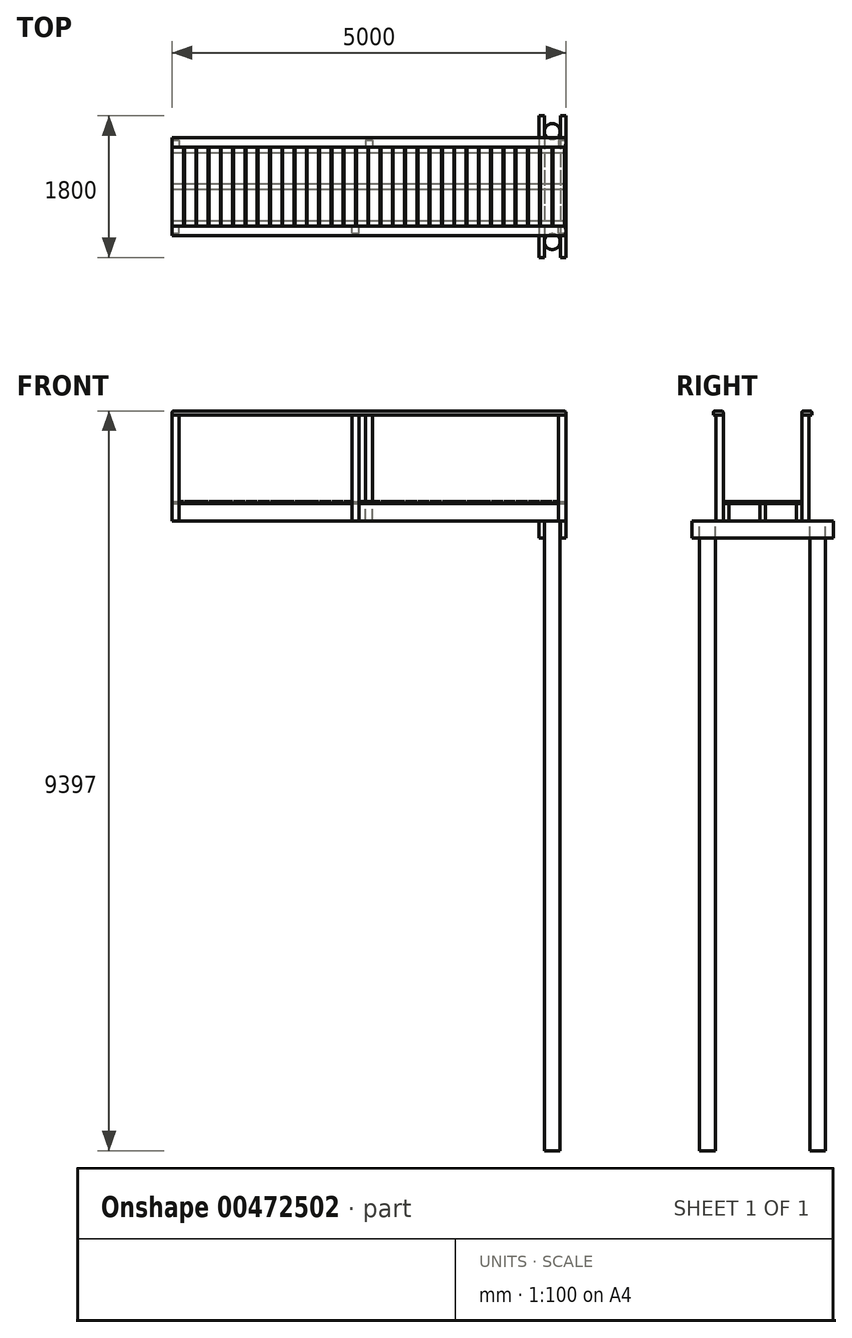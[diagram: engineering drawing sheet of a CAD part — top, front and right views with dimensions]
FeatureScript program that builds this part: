
annotation { "Feature Type Name" : "Feature", "Feature Type Description" : "" }
export const myFeature = defineFeature(function(context is Context, id is Id, definition is map)
    precondition{}
    {
        {
            var Q0;
            Q0=qCreatedBy(makeId("Top.planeOp"),FACE);
            var sketch = newSketch(context, id + "F0", { "sketchPlane" : qUnion([Q0])});
            skCircle(sketch, "E0", {"center": v(-387.32, 554.23) * mm, "radius": 100 * mm});
            skCircle(sketch, "E1", {"center": v(-387.32, -845.77) * mm, "radius": 100 * mm});
            skSolve(sketch);
        }
        {
            var Q0;
            Q0=qCreatedBy(makeId("Top.planeOp"),FACE);
            var sketch = newSketch(context, id + "F1", { "sketchPlane" : qUnion([Q0])});
            skLineSegment(sketch, "E2.bottom", {"start": v(-557.32, 754.23) * mm, "end": v(-487.32, 754.23) * mm});
            skLineSegment(sketch, "E2.top", {"start": v(-557.32, -1045.77) * mm, "end": v(-487.32, -1045.77) * mm});
            skLineSegment(sketch, "E2.left", {"start": v(-557.32, 754.23) * mm, "end": v(-557.32, -1045.77) * mm});
            skLineSegment(sketch, "E2.right", {"start": v(-487.32, 754.23) * mm, "end": v(-487.32, -1045.77) * mm});
            skLineSegment(sketch, "E3.left", {"start": v(-557.32, 754.23) * mm, "end": v(-557.32, 754.23) * mm});
            skLineSegment(sketch, "E3.right", {"start": v(-487.32, 754.23) * mm, "end": v(-487.32, 754.23) * mm});
            skLineSegment(sketch, "E4.MirrorCS", {"start": v(-285.72, 754.23) * mm, "end": v(-285.72, -1045.77) * mm});
            skLineSegment(sketch, "E5.MirrorCS", {"start": v(-215.72, 754.23) * mm, "end": v(-215.72, -1045.77) * mm});
            skLineSegment(sketch, "E6.MirrorCS", {"start": v(-215.72, 754.23) * mm, "end": v(-285.72, 754.23) * mm});
            skLineSegment(sketch, "E7.MirrorCS", {"start": v(-215.72, -1045.77) * mm, "end": v(-285.72, -1045.77) * mm});
            skSolve(sketch);
        }
        {
            var Q0;
            Q0=qSketchRegion(id+"F0",true);
            extrude(context, id + "F2", {"entities" : qUnion([Q0]), "oppositeDirection" : true, "depth" : 8000 * mm});
        }
        {
            var Q0;
            Q0=qSketchRegion(id+"F1",true);
            extrude(context, id + "F3", {"entities" : qUnion([Q0]), "oppositeDirection" : true, "depth" : 220 * mm});
        }
        {
            var Q0;
            Q0=qCreatedBy(makeId("Top.planeOp"),FACE);
            var sketch = newSketch(context, id + "F4", { "sketchPlane" : qUnion([Q0])});
            skLineSegment(sketch, "E8.bottom", {"start": v(-5215.72, 354.23) * mm, "end": v(-215.72, 354.23) * mm});
            skLineSegment(sketch, "E8.top", {"start": v(-5215.72, 284.23) * mm, "end": v(-215.72, 284.23) * mm});
            skLineSegment(sketch, "E8.left", {"start": v(-5215.72, 354.23) * mm, "end": v(-5215.72, 284.23) * mm});
            skLineSegment(sketch, "E8.right", {"start": v(-215.72, 354.23) * mm, "end": v(-215.72, 284.23) * mm});
            skLineSegment(sketch, "E9.0.1.0", {"start": v(-5215.72, -110.77) * mm, "end": v(-215.72, -110.77) * mm});
            skLineSegment(sketch, "E9.0.1.1", {"start": v(-5215.72, -180.77) * mm, "end": v(-215.72, -180.77) * mm});
            skLineSegment(sketch, "E9.0.1.2", {"start": v(-215.72, -110.77) * mm, "end": v(-215.72, -180.77) * mm});
            skLineSegment(sketch, "E9.0.1.3", {"start": v(-5215.72, -110.77) * mm, "end": v(-5215.72, -180.77) * mm});
            skLineSegment(sketch, "E9.0.2.0", {"start": v(-5215.72, -575.77) * mm, "end": v(-215.72, -575.77) * mm});
            skLineSegment(sketch, "E9.0.2.1", {"start": v(-5215.72, -645.77) * mm, "end": v(-215.72, -645.77) * mm});
            skLineSegment(sketch, "E9.0.2.2", {"start": v(-215.72, -575.77) * mm, "end": v(-215.72, -645.77) * mm});
            skLineSegment(sketch, "E9.0.2.3", {"start": v(-5215.72, -575.77) * mm, "end": v(-5215.72, -645.77) * mm});
            skLineSegment(sketch, "E9.direction1", {"start": v(-5387.32, 354.23) * mm, "end": v(-5215.72, 354.23) * mm, "construction": true});
            skLineSegment(sketch, "E9.direction2", {"start": v(-5215.72, 354.23) * mm, "end": v(-5215.72, -110.77) * mm, "construction": true});
            skSolve(sketch);
        }
        {
            var Q0;
            Q0=makeQuery(id+"F4.imprint","IMPRINT",FACE,{"disambiguationData":[TD([[makeQuery(id+"F4.imprint","IMPRINT",EDGE,{"derivedFrom":sQuery(id+"F4.wireOp",EDGE,"E8.bottom")}),-1.0]])]});
            var Q1;
            Q1=makeQuery(id+"F4.imprint","IMPRINT",FACE,{"disambiguationData":[TD([[makeQuery(id+"F4.imprint","IMPRINT",EDGE,{"derivedFrom":sQuery(id+"F4.wireOp",EDGE,"E9.0.2.0")}),-1.0]])]});
            var Q2;
            Q2=makeQuery(id+"F4.imprint","IMPRINT",FACE,{"disambiguationData":[TD([[makeQuery(id+"F4.imprint","IMPRINT",EDGE,{"derivedFrom":sQuery(id+"F4.wireOp",EDGE,"E9.0.1.0")}),-1.0]])]});
            extrude(context, id + "F5", {"entities" : qUnion([Q0, Q1, Q2]), "depth" : 220 * mm});
        }
        {
            var Q0;
            Q0=makeQuery(id+"F5.opExtrude","CAP_FACE",FACE,{"disambiguationData":[OSD([sQuery(id+"F4.wireOp",EDGE,"E8.bottom"),sQuery(id+"F4.wireOp",EDGE,"E8.top"),sQuery(id+"F4.wireOp",EDGE,"E8.left"),sQuery(id+"F4.wireOp",EDGE,"E8.right")])],"isStart":false});
            var sketch = newSketch(context, id + "F6", { "sketchPlane" : qUnion([Q0])});
            skLineSegment(sketch, "E10.bottom", {"start": v(-5215.72, 354.23) * mm, "end": v(-5070.72, 354.23) * mm});
            skLineSegment(sketch, "E10.top", {"start": v(-5215.72, -645.77) * mm, "end": v(-5070.72, -645.77) * mm});
            skLineSegment(sketch, "E10.left", {"start": v(-5215.72, 354.23) * mm, "end": v(-5215.72, -645.77) * mm});
            skLineSegment(sketch, "E10.right", {"start": v(-5070.72, 354.23) * mm, "end": v(-5070.72, -645.77) * mm});
            skLineSegment(sketch, "E11.1.0.0", {"start": v(-4914.72, 354.23) * mm, "end": v(-4914.72, -645.77) * mm});
            skLineSegment(sketch, "E11.1.0.1", {"start": v(-5059.72, 354.23) * mm, "end": v(-4914.72, 354.23) * mm});
            skLineSegment(sketch, "E11.1.0.2", {"start": v(-5059.72, 354.23) * mm, "end": v(-5059.72, -645.77) * mm});
            skLineSegment(sketch, "E11.1.0.3", {"start": v(-5059.72, -645.77) * mm, "end": v(-4914.72, -645.77) * mm});
            skLineSegment(sketch, "E11.2.0.0", {"start": v(-4758.72, 354.23) * mm, "end": v(-4758.72, -645.77) * mm});
            skLineSegment(sketch, "E11.2.0.1", {"start": v(-4903.72, 354.23) * mm, "end": v(-4758.72, 354.23) * mm});
            skLineSegment(sketch, "E11.2.0.2", {"start": v(-4903.72, 354.23) * mm, "end": v(-4903.72, -645.77) * mm});
            skLineSegment(sketch, "E11.2.0.3", {"start": v(-4903.72, -645.77) * mm, "end": v(-4758.72, -645.77) * mm});
            skLineSegment(sketch, "E11.3.0.0", {"start": v(-4602.72, 354.23) * mm, "end": v(-4602.72, -645.77) * mm});
            skLineSegment(sketch, "E11.3.0.1", {"start": v(-4747.72, 354.23) * mm, "end": v(-4602.72, 354.23) * mm});
            skLineSegment(sketch, "E11.3.0.2", {"start": v(-4747.72, 354.23) * mm, "end": v(-4747.72, -645.77) * mm});
            skLineSegment(sketch, "E11.3.0.3", {"start": v(-4747.72, -645.77) * mm, "end": v(-4602.72, -645.77) * mm});
            skLineSegment(sketch, "E11.4.0.0", {"start": v(-4446.72, 354.23) * mm, "end": v(-4446.72, -645.77) * mm});
            skLineSegment(sketch, "E11.4.0.1", {"start": v(-4591.72, 354.23) * mm, "end": v(-4446.72, 354.23) * mm});
            skLineSegment(sketch, "E11.4.0.2", {"start": v(-4591.72, 354.23) * mm, "end": v(-4591.72, -645.77) * mm});
            skLineSegment(sketch, "E11.4.0.3", {"start": v(-4591.72, -645.77) * mm, "end": v(-4446.72, -645.77) * mm});
            skLineSegment(sketch, "E11.5.0.0", {"start": v(-4290.72, 354.23) * mm, "end": v(-4290.72, -645.77) * mm});
            skLineSegment(sketch, "E11.5.0.1", {"start": v(-4435.72, 354.23) * mm, "end": v(-4290.72, 354.23) * mm});
            skLineSegment(sketch, "E11.5.0.2", {"start": v(-4435.72, 354.23) * mm, "end": v(-4435.72, -645.77) * mm});
            skLineSegment(sketch, "E11.5.0.3", {"start": v(-4435.72, -645.77) * mm, "end": v(-4290.72, -645.77) * mm});
            skLineSegment(sketch, "E11.6.0.0", {"start": v(-4134.72, 354.23) * mm, "end": v(-4134.72, -645.77) * mm});
            skLineSegment(sketch, "E11.6.0.1", {"start": v(-4279.72, 354.23) * mm, "end": v(-4134.72, 354.23) * mm});
            skLineSegment(sketch, "E11.6.0.2", {"start": v(-4279.72, 354.23) * mm, "end": v(-4279.72, -645.77) * mm});
            skLineSegment(sketch, "E11.6.0.3", {"start": v(-4279.72, -645.77) * mm, "end": v(-4134.72, -645.77) * mm});
            skLineSegment(sketch, "E11.7.0.0", {"start": v(-3978.72, 354.23) * mm, "end": v(-3978.72, -645.77) * mm});
            skLineSegment(sketch, "E11.7.0.1", {"start": v(-4123.72, 354.23) * mm, "end": v(-3978.72, 354.23) * mm});
            skLineSegment(sketch, "E11.7.0.2", {"start": v(-4123.72, 354.23) * mm, "end": v(-4123.72, -645.77) * mm});
            skLineSegment(sketch, "E11.7.0.3", {"start": v(-4123.72, -645.77) * mm, "end": v(-3978.72, -645.77) * mm});
            skLineSegment(sketch, "E11.8.0.0", {"start": v(-3822.72, 354.23) * mm, "end": v(-3822.72, -645.77) * mm});
            skLineSegment(sketch, "E11.8.0.1", {"start": v(-3967.72, 354.23) * mm, "end": v(-3822.72, 354.23) * mm});
            skLineSegment(sketch, "E11.8.0.2", {"start": v(-3967.72, 354.23) * mm, "end": v(-3967.72, -645.77) * mm});
            skLineSegment(sketch, "E11.8.0.3", {"start": v(-3967.72, -645.77) * mm, "end": v(-3822.72, -645.77) * mm});
            skLineSegment(sketch, "E11.9.0.0", {"start": v(-3666.72, 354.23) * mm, "end": v(-3666.72, -645.77) * mm});
            skLineSegment(sketch, "E11.9.0.1", {"start": v(-3811.72, 354.23) * mm, "end": v(-3666.72, 354.23) * mm});
            skLineSegment(sketch, "E11.9.0.2", {"start": v(-3811.72, 354.23) * mm, "end": v(-3811.72, -645.77) * mm});
            skLineSegment(sketch, "E11.9.0.3", {"start": v(-3811.72, -645.77) * mm, "end": v(-3666.72, -645.77) * mm});
            skLineSegment(sketch, "E11.10.0.0", {"start": v(-3510.72, 354.23) * mm, "end": v(-3510.72, -645.77) * mm});
            skLineSegment(sketch, "E11.10.0.1", {"start": v(-3655.72, 354.23) * mm, "end": v(-3510.72, 354.23) * mm});
            skLineSegment(sketch, "E11.10.0.2", {"start": v(-3655.72, 354.23) * mm, "end": v(-3655.72, -645.77) * mm});
            skLineSegment(sketch, "E11.10.0.3", {"start": v(-3655.72, -645.77) * mm, "end": v(-3510.72, -645.77) * mm});
            skLineSegment(sketch, "E11.11.0.0", {"start": v(-3354.72, 354.23) * mm, "end": v(-3354.72, -645.77) * mm});
            skLineSegment(sketch, "E11.11.0.1", {"start": v(-3499.72, 354.23) * mm, "end": v(-3354.72, 354.23) * mm});
            skLineSegment(sketch, "E11.11.0.2", {"start": v(-3499.72, 354.23) * mm, "end": v(-3499.72, -645.77) * mm});
            skLineSegment(sketch, "E11.11.0.3", {"start": v(-3499.72, -645.77) * mm, "end": v(-3354.72, -645.77) * mm});
            skLineSegment(sketch, "E11.12.0.0", {"start": v(-3198.72, 354.23) * mm, "end": v(-3198.72, -645.77) * mm});
            skLineSegment(sketch, "E11.12.0.1", {"start": v(-3343.72, 354.23) * mm, "end": v(-3198.72, 354.23) * mm});
            skLineSegment(sketch, "E11.12.0.2", {"start": v(-3343.72, 354.23) * mm, "end": v(-3343.72, -645.77) * mm});
            skLineSegment(sketch, "E11.12.0.3", {"start": v(-3343.72, -645.77) * mm, "end": v(-3198.72, -645.77) * mm});
            skLineSegment(sketch, "E11.13.0.0", {"start": v(-3042.72, 354.23) * mm, "end": v(-3042.72, -645.77) * mm});
            skLineSegment(sketch, "E11.13.0.1", {"start": v(-3187.72, 354.23) * mm, "end": v(-3042.72, 354.23) * mm});
            skLineSegment(sketch, "E11.13.0.2", {"start": v(-3187.72, 354.23) * mm, "end": v(-3187.72, -645.77) * mm});
            skLineSegment(sketch, "E11.13.0.3", {"start": v(-3187.72, -645.77) * mm, "end": v(-3042.72, -645.77) * mm});
            skLineSegment(sketch, "E11.14.0.0", {"start": v(-2886.72, 354.23) * mm, "end": v(-2886.72, -645.77) * mm});
            skLineSegment(sketch, "E11.14.0.1", {"start": v(-3031.72, 354.23) * mm, "end": v(-2886.72, 354.23) * mm});
            skLineSegment(sketch, "E11.14.0.2", {"start": v(-3031.72, 354.23) * mm, "end": v(-3031.72, -645.77) * mm});
            skLineSegment(sketch, "E11.14.0.3", {"start": v(-3031.72, -645.77) * mm, "end": v(-2886.72, -645.77) * mm});
            skLineSegment(sketch, "E11.15.0.0", {"start": v(-2730.72, 354.23) * mm, "end": v(-2730.72, -645.77) * mm});
            skLineSegment(sketch, "E11.15.0.1", {"start": v(-2875.72, 354.23) * mm, "end": v(-2730.72, 354.23) * mm});
            skLineSegment(sketch, "E11.15.0.2", {"start": v(-2875.72, 354.23) * mm, "end": v(-2875.72, -645.77) * mm});
            skLineSegment(sketch, "E11.15.0.3", {"start": v(-2875.72, -645.77) * mm, "end": v(-2730.72, -645.77) * mm});
            skLineSegment(sketch, "E11.16.0.0", {"start": v(-2574.72, 354.23) * mm, "end": v(-2574.72, -645.77) * mm});
            skLineSegment(sketch, "E11.16.0.1", {"start": v(-2719.72, 354.23) * mm, "end": v(-2574.72, 354.23) * mm});
            skLineSegment(sketch, "E11.16.0.2", {"start": v(-2719.72, 354.23) * mm, "end": v(-2719.72, -645.77) * mm});
            skLineSegment(sketch, "E11.16.0.3", {"start": v(-2719.72, -645.77) * mm, "end": v(-2574.72, -645.77) * mm});
            skLineSegment(sketch, "E11.17.0.0", {"start": v(-2418.72, 354.23) * mm, "end": v(-2418.72, -645.77) * mm});
            skLineSegment(sketch, "E11.17.0.1", {"start": v(-2563.72, 354.23) * mm, "end": v(-2418.72, 354.23) * mm});
            skLineSegment(sketch, "E11.17.0.2", {"start": v(-2563.72, 354.23) * mm, "end": v(-2563.72, -645.77) * mm});
            skLineSegment(sketch, "E11.17.0.3", {"start": v(-2563.72, -645.77) * mm, "end": v(-2418.72, -645.77) * mm});
            skLineSegment(sketch, "E11.18.0.0", {"start": v(-2262.72, 354.23) * mm, "end": v(-2262.72, -645.77) * mm});
            skLineSegment(sketch, "E11.18.0.1", {"start": v(-2407.72, 354.23) * mm, "end": v(-2262.72, 354.23) * mm});
            skLineSegment(sketch, "E11.18.0.2", {"start": v(-2407.72, 354.23) * mm, "end": v(-2407.72, -645.77) * mm});
            skLineSegment(sketch, "E11.18.0.3", {"start": v(-2407.72, -645.77) * mm, "end": v(-2262.72, -645.77) * mm});
            skLineSegment(sketch, "E11.19.0.0", {"start": v(-2106.72, 354.23) * mm, "end": v(-2106.72, -645.77) * mm});
            skLineSegment(sketch, "E11.19.0.1", {"start": v(-2251.72, 354.23) * mm, "end": v(-2106.72, 354.23) * mm});
            skLineSegment(sketch, "E11.19.0.2", {"start": v(-2251.72, 354.23) * mm, "end": v(-2251.72, -645.77) * mm});
            skLineSegment(sketch, "E11.19.0.3", {"start": v(-2251.72, -645.77) * mm, "end": v(-2106.72, -645.77) * mm});
            skLineSegment(sketch, "E11.20.0.0", {"start": v(-1950.72, 354.23) * mm, "end": v(-1950.72, -645.77) * mm});
            skLineSegment(sketch, "E11.20.0.1", {"start": v(-2095.72, 354.23) * mm, "end": v(-1950.72, 354.23) * mm});
            skLineSegment(sketch, "E11.20.0.2", {"start": v(-2095.72, 354.23) * mm, "end": v(-2095.72, -645.77) * mm});
            skLineSegment(sketch, "E11.20.0.3", {"start": v(-2095.72, -645.77) * mm, "end": v(-1950.72, -645.77) * mm});
            skLineSegment(sketch, "E11.21.0.0", {"start": v(-1794.72, 354.23) * mm, "end": v(-1794.72, -645.77) * mm});
            skLineSegment(sketch, "E11.21.0.1", {"start": v(-1939.72, 354.23) * mm, "end": v(-1794.72, 354.23) * mm});
            skLineSegment(sketch, "E11.21.0.2", {"start": v(-1939.72, 354.23) * mm, "end": v(-1939.72, -645.77) * mm});
            skLineSegment(sketch, "E11.21.0.3", {"start": v(-1939.72, -645.77) * mm, "end": v(-1794.72, -645.77) * mm});
            skLineSegment(sketch, "E11.22.0.0", {"start": v(-1638.72, 354.23) * mm, "end": v(-1638.72, -645.77) * mm});
            skLineSegment(sketch, "E11.22.0.1", {"start": v(-1783.72, 354.23) * mm, "end": v(-1638.72, 354.23) * mm});
            skLineSegment(sketch, "E11.22.0.2", {"start": v(-1783.72, 354.23) * mm, "end": v(-1783.72, -645.77) * mm});
            skLineSegment(sketch, "E11.22.0.3", {"start": v(-1783.72, -645.77) * mm, "end": v(-1638.72, -645.77) * mm});
            skLineSegment(sketch, "E11.23.0.0", {"start": v(-1482.72, 354.23) * mm, "end": v(-1482.72, -645.77) * mm});
            skLineSegment(sketch, "E11.23.0.1", {"start": v(-1627.72, 354.23) * mm, "end": v(-1482.72, 354.23) * mm});
            skLineSegment(sketch, "E11.23.0.2", {"start": v(-1627.72, 354.23) * mm, "end": v(-1627.72, -645.77) * mm});
            skLineSegment(sketch, "E11.23.0.3", {"start": v(-1627.72, -645.77) * mm, "end": v(-1482.72, -645.77) * mm});
            skLineSegment(sketch, "E11.24.0.0", {"start": v(-1326.72, 354.23) * mm, "end": v(-1326.72, -645.77) * mm});
            skLineSegment(sketch, "E11.24.0.1", {"start": v(-1471.72, 354.23) * mm, "end": v(-1326.72, 354.23) * mm});
            skLineSegment(sketch, "E11.24.0.2", {"start": v(-1471.72, 354.23) * mm, "end": v(-1471.72, -645.77) * mm});
            skLineSegment(sketch, "E11.24.0.3", {"start": v(-1471.72, -645.77) * mm, "end": v(-1326.72, -645.77) * mm});
            skLineSegment(sketch, "E11.25.0.0", {"start": v(-1170.72, 354.23) * mm, "end": v(-1170.72, -645.77) * mm});
            skLineSegment(sketch, "E11.25.0.1", {"start": v(-1315.72, 354.23) * mm, "end": v(-1170.72, 354.23) * mm});
            skLineSegment(sketch, "E11.25.0.2", {"start": v(-1315.72, 354.23) * mm, "end": v(-1315.72, -645.77) * mm});
            skLineSegment(sketch, "E11.25.0.3", {"start": v(-1315.72, -645.77) * mm, "end": v(-1170.72, -645.77) * mm});
            skLineSegment(sketch, "E11.26.0.0", {"start": v(-1014.72, 354.23) * mm, "end": v(-1014.72, -645.77) * mm});
            skLineSegment(sketch, "E11.26.0.1", {"start": v(-1159.72, 354.23) * mm, "end": v(-1014.72, 354.23) * mm});
            skLineSegment(sketch, "E11.26.0.2", {"start": v(-1159.72, 354.23) * mm, "end": v(-1159.72, -645.77) * mm});
            skLineSegment(sketch, "E11.26.0.3", {"start": v(-1159.72, -645.77) * mm, "end": v(-1014.72, -645.77) * mm});
            skLineSegment(sketch, "E11.27.0.0", {"start": v(-858.72, 354.23) * mm, "end": v(-858.72, -645.77) * mm});
            skLineSegment(sketch, "E11.27.0.1", {"start": v(-1003.72, 354.23) * mm, "end": v(-858.72, 354.23) * mm});
            skLineSegment(sketch, "E11.27.0.2", {"start": v(-1003.72, 354.23) * mm, "end": v(-1003.72, -645.77) * mm});
            skLineSegment(sketch, "E11.27.0.3", {"start": v(-1003.72, -645.77) * mm, "end": v(-858.72, -645.77) * mm});
            skLineSegment(sketch, "E11.28.0.0", {"start": v(-702.72, 354.23) * mm, "end": v(-702.72, -645.77) * mm});
            skLineSegment(sketch, "E11.28.0.1", {"start": v(-847.72, 354.23) * mm, "end": v(-702.72, 354.23) * mm});
            skLineSegment(sketch, "E11.28.0.2", {"start": v(-847.72, 354.23) * mm, "end": v(-847.72, -645.77) * mm});
            skLineSegment(sketch, "E11.28.0.3", {"start": v(-847.72, -645.77) * mm, "end": v(-702.72, -645.77) * mm});
            skLineSegment(sketch, "E11.29.0.0", {"start": v(-546.72, 354.23) * mm, "end": v(-546.72, -645.77) * mm});
            skLineSegment(sketch, "E11.29.0.1", {"start": v(-691.72, 354.23) * mm, "end": v(-546.72, 354.23) * mm});
            skLineSegment(sketch, "E11.29.0.2", {"start": v(-691.72, 354.23) * mm, "end": v(-691.72, -645.77) * mm});
            skLineSegment(sketch, "E11.29.0.3", {"start": v(-691.72, -645.77) * mm, "end": v(-546.72, -645.77) * mm});
            skLineSegment(sketch, "E11.30.0.0", {"start": v(-390.72, 354.23) * mm, "end": v(-390.72, -645.77) * mm});
            skLineSegment(sketch, "E11.30.0.1", {"start": v(-535.72, 354.23) * mm, "end": v(-390.72, 354.23) * mm});
            skLineSegment(sketch, "E11.30.0.2", {"start": v(-535.72, 354.23) * mm, "end": v(-535.72, -645.77) * mm});
            skLineSegment(sketch, "E11.30.0.3", {"start": v(-535.72, -645.77) * mm, "end": v(-390.72, -645.77) * mm});
            skLineSegment(sketch, "E11.31.0.0", {"start": v(-234.72, 354.23) * mm, "end": v(-234.72, -645.77) * mm});
            skLineSegment(sketch, "E11.31.0.1", {"start": v(-379.72, 354.23) * mm, "end": v(-234.72, 354.23) * mm});
            skLineSegment(sketch, "E11.31.0.2", {"start": v(-379.72, 354.23) * mm, "end": v(-379.72, -645.77) * mm});
            skLineSegment(sketch, "E11.31.0.3", {"start": v(-379.72, -645.77) * mm, "end": v(-234.72, -645.77) * mm});
            skLineSegment(sketch, "E11.direction1", {"start": v(-5070.72, -645.77) * mm, "end": v(-4914.72, -645.77) * mm, "construction": true});
            skSolve(sketch);
        }
        {
            var Q0;
            Q0=qSketchRegion(id+"F6",true);
            extrude(context, id + "F7", {"entities" : qUnion([Q0]), "depth" : 27 * mm});
        }
        {
            var Q0;
            Q0=makeQuery(id+"F5.opExtrude","SWEPT_FACE",FACE,{"disambiguationData":[OSD([sQuery(id+"F4.wireOp",EDGE,"E9.0.2.1")])]});
            var sketch = newSketch(context, id + "F8", { "sketchPlane" : qUnion([Q0])});
            skLineSegment(sketch, "E12.bottom", {"start": v(-5215.72, 0) * mm, "end": v(-5125.72, 0) * mm});
            skLineSegment(sketch, "E12.top", {"start": v(-5215.72, 1347) * mm, "end": v(-5125.72, 1347) * mm});
            skLineSegment(sketch, "E12.left", {"start": v(-5215.72, 0) * mm, "end": v(-5215.72, 1347) * mm});
            skLineSegment(sketch, "E12.right", {"start": v(-5125.72, 0) * mm, "end": v(-5125.72, 1347) * mm});
            skLineSegment(sketch, "E13.bottom", {"start": v(-215.72, 0) * mm, "end": v(-305.72, 0) * mm});
            skLineSegment(sketch, "E13.top", {"start": v(-215.72, 1347) * mm, "end": v(-305.72, 1347) * mm});
            skLineSegment(sketch, "E13.left", {"start": v(-215.72, 0) * mm, "end": v(-215.72, 1347) * mm});
            skLineSegment(sketch, "E13.right", {"start": v(-305.72, 0) * mm, "end": v(-305.72, 1347) * mm});
            skLineSegment(sketch, "E14.bottom", {"start": v(-2932.32, 1347) * mm, "end": v(-2842.32, 1347) * mm});
            skLineSegment(sketch, "E14.top", {"start": v(-2932.32, 0) * mm, "end": v(-2842.32, 0) * mm});
            skLineSegment(sketch, "E14.left", {"start": v(-2842.32, 1347) * mm, "end": v(-2842.32, 0) * mm});
            skLineSegment(sketch, "E14.right", {"start": v(-2932.32, 1347) * mm, "end": v(-2932.32, 0) * mm});
            skSolve(sketch);
        }
        {
            var Q0;
            Q0=qSketchRegion(id+"F8",true);
            extrude(context, id + "F9", {"entities" : qUnion([Q0]), "depth" : 90 * mm});
        }
        {
            var Q0;
            Q0=makeQuery(id+"F5.opExtrude","SWEPT_FACE",FACE,{"disambiguationData":[OSD([sQuery(id+"F4.wireOp",EDGE,"E8.bottom")])]});
            var sketch = newSketch(context, id + "F10", { "sketchPlane" : qUnion([Q0])});
            skLineSegment(sketch, "E15.bottom", {"start": v(5215.72, 0) * mm, "end": v(5125.72, 0) * mm});
            skLineSegment(sketch, "E15.top", {"start": v(5215.72, 1347) * mm, "end": v(5125.72, 1347) * mm});
            skLineSegment(sketch, "E15.left", {"start": v(5215.72, 0) * mm, "end": v(5215.72, 1347) * mm});
            skLineSegment(sketch, "E15.right", {"start": v(5125.72, 0) * mm, "end": v(5125.72, 1347) * mm});
            skLineSegment(sketch, "E16.1.0.0", {"start": v(2670.72, 0) * mm, "end": v(2670.72, 1347) * mm});
            skLineSegment(sketch, "E16.1.0.1", {"start": v(2760.72, 1347) * mm, "end": v(2670.72, 1347) * mm});
            skLineSegment(sketch, "E16.1.0.2", {"start": v(2760.72, 0) * mm, "end": v(2760.72, 1347) * mm});
            skLineSegment(sketch, "E16.1.0.3", {"start": v(2760.72, 0) * mm, "end": v(2670.72, 0) * mm});
            skLineSegment(sketch, "E16.2.0.0", {"start": v(215.72, 0) * mm, "end": v(215.72, 1347) * mm});
            skLineSegment(sketch, "E16.2.0.1", {"start": v(305.72, 1347) * mm, "end": v(215.72, 1347) * mm});
            skLineSegment(sketch, "E16.2.0.2", {"start": v(305.72, 0) * mm, "end": v(305.72, 1347) * mm});
            skLineSegment(sketch, "E16.2.0.3", {"start": v(305.72, 0) * mm, "end": v(215.72, 0) * mm});
            skLineSegment(sketch, "E16.direction1", {"start": v(5125.72, 0) * mm, "end": v(2670.72, 0) * mm, "construction": true});
            skSolve(sketch);
        }
        {
            var Q0;
            Q0=qSketchRegion(id+"F10",true);
            extrude(context, id + "F11", {"entities" : qUnion([Q0]), "depth" : 90 * mm});
        }
        {
            var Q0;
            Q0=makeQuery(id+"F11.opExtrude","SWEPT_FACE",FACE,{"disambiguationData":[OSD([sQuery(id+"F10.wireOp",EDGE,"E15.top")])]});
            var sketch = newSketch(context, id + "F12", { "sketchPlane" : qUnion([Q0])});
            skLineSegment(sketch, "E17.bottom", {"start": v(-5215.72, 479.23) * mm, "end": v(-215.72, 479.23) * mm});
            skLineSegment(sketch, "E17.top", {"start": v(-5215.72, 354.23) * mm, "end": v(-215.72, 354.23) * mm});
            skLineSegment(sketch, "E17.left", {"start": v(-5215.72, 479.23) * mm, "end": v(-5215.72, 354.23) * mm});
            skLineSegment(sketch, "E17.right", {"start": v(-215.72, 479.23) * mm, "end": v(-215.72, 354.23) * mm});
            skLineSegment(sketch, "E18.MirrorCS", {"start": v(-5215.72, -770.77) * mm, "end": v(-215.72, -770.77) * mm});
            skLineSegment(sketch, "E19.MirrorCS", {"start": v(-5215.72, -645.77) * mm, "end": v(-215.72, -645.77) * mm});
            skLineSegment(sketch, "E20.MirrorCS", {"start": v(-5215.72, -770.77) * mm, "end": v(-5215.72, -645.77) * mm});
            skLineSegment(sketch, "E21.MirrorCS", {"start": v(-215.72, -770.77) * mm, "end": v(-215.72, -645.77) * mm});
            skSolve(sketch);
        }
        {
            var Q0;
            Q0=qSketchRegion(id+"F12",true);
            extrude(context, id + "F13", {"entities" : qUnion([Q0]), "depth" : 50 * mm});
        }
        {
            var Q0;
            Q0=makeQuery(id+"F13.opExtrude","CAP_EDGE",EDGE,{"disambiguationData":[OSD([sQuery(id+"F12.wireOp",EDGE,"E17.bottom")])],"isStart":false});
            var Q1;
            Q1=makeQuery(id+"F13.opExtrude","CAP_EDGE",EDGE,{"disambiguationData":[OSD([sQuery(id+"F12.wireOp",EDGE,"E18.MirrorCS")])],"isStart":false});
            var Q2;
            Q2=makeQuery(id+"F13.opExtrude","CAP_EDGE",EDGE,{"disambiguationData":[OSD([sQuery(id+"F12.wireOp",EDGE,"E20.MirrorCS")])],"isStart":false});
            var Q3;
            Q3=makeQuery(id+"F13.opExtrude","CAP_EDGE",EDGE,{"disambiguationData":[OSD([sQuery(id+"F12.wireOp",EDGE,"E17.top")])],"isStart":false});
            var Q4;
            Q4=makeQuery(id+"F13.opExtrude","CAP_EDGE",EDGE,{"disambiguationData":[OSD([sQuery(id+"F12.wireOp",EDGE,"E17.left")])],"isStart":false});
            var Q5;
            Q5=makeQuery(id+"F13.opExtrude","CAP_EDGE",EDGE,{"disambiguationData":[OSD([sQuery(id+"F12.wireOp",EDGE,"E17.right")])],"isStart":false});
            var Q6;
            Q6=makeQuery(id+"F13.opExtrude","CAP_EDGE",EDGE,{"disambiguationData":[OSD([sQuery(id+"F12.wireOp",EDGE,"E19.MirrorCS")])],"isStart":false});
            var Q7;
            Q7=makeQuery(id+"F13.opExtrude","CAP_EDGE",EDGE,{"disambiguationData":[OSD([sQuery(id+"F12.wireOp",EDGE,"E21.MirrorCS")])],"isStart":false});
            fillet(context, id + "F14", {"entities" : qUnion([Q0, Q1, Q2, Q3, Q4, Q5, Q6, Q7]), "radius" : 20 * mm, "tangentPropagation" : true, "allowEdgeOverflow" : false});
        }
    });
